# Revit family: xTrench_Drain-Jay R. Smith-9812BS
name_source: partatom
category: Plumbing Fixtures
units: mm (PartAtom-declared; Revit-internal decimal feet)

## family parameters
Always vertical = No
Cut with Voids When Loaded = No
OmniClass Number = 23.70.50.21.24
OmniClass Title = Waste Water Drains
Part Type = Normal
Room Calculation Point = No
Round Connector Dimension = Use Diameter
Shared = Yes
Work Plane-Based = Yes

## types (20) — shared parameters
Assembly Code = D2030300
Body Material = Polyester-Jay R. Smith-Fiberglass
Bottom Outlet = Yes
Bottom Outlet (Specify) = 4 "
CW Connection = No
Description = 10-inch WIDE HIGH CAPACITY PRE-SLOPED FIBERGLASS TRENCH DRAIN SYSTEM
Ductile Iron Slotted Grate = No
End Cap Right = No
Galvanized Steel Bar Grate = No
HW Connection = No
Horizontal Inlet Cap = No
Horizontal Outlet Cap = No
Inlet Size (Specify) = 4 "
Manufacturer = Jay R. Smith
Model = 9812
Opening Inner Rad = 2 "
Opening Outer Rad = 2.25 "
Product Documentation Link = https://www.jrsmith.com
Product URL = https://www.jrsmith.com
Stainless Steel Bar Grate = No
Type Comments = 10-inch WIDE HIGH CAPACITY PRE-SLOPED FIBERGLASS
URL = http://www.jrsmith.com
Universal Deep Closing End Cap = No
Universal Shallow Closing End Cap = No
Vent Connection = No
Waste Connection = Yes
zero-valued in all types: Default Elevation

## per-type parameters (varying)
| type | 108 Channel Rebar | 3N3 Rebar | Bottom Outlet Dist. from Front Inlet | Deep End Depth | J Bend Anchor | Outlet Size (Specify) | Shallow End Depth | Total Length |
| 9812-801 | Yes | No | 59 " | 8 " | Yes | 4 " | 6.88 " | 108 " |
| 9812-802 | Yes | No | 59 " | 9.13 " | Yes | 0 " | 8 " | 108 " |
| 9812-803 | Yes | No | 59 " | 10.25 " | Yes | 0 " | 9.13 " | 108 " |
| 9812-803N | Yes | No | 59 " | 10.25 " | Yes | 0 " | 10.25 " | 108 " |
| 9812-804 | Yes | No | 59 " | 11.38 " | Yes | 0 " | 10.25 " | 108 " |
| 9812-805 | Yes | No | 59 " | 12.5 " | Yes | 0 " | 11.38 " | 108 " |
| 9812-806 | Yes | No | 59 " | 13.63 " | Yes | 0 " | 12.5 " | 108 " |
| 9812-806N | Yes | No | 59 " | 13.63 " | Yes | 0 " | 13.63 " | 108 " |
| 9812-807 | Yes | No | 59 " | 14.75 " | Yes | 0 " | 13.63 " | 108 " |
| 9812-808 | Yes | No | 59 " | 15.88 " | Yes | 0 " | 14.75 " | 108 " |
| 9812-809N | Yes | No | 59 " | 17 " | Yes | 0 " | 17 " | 108 " |
| 9812-810 | Yes | No | 59 " | 18.13 " | Yes | 0 " | 17 " | 108 " |
| 9812-811 | Yes | No | 59 " | 19.25 " | Yes | 0 " | 18.13 " | 108 " |
| 9812-812 | Yes | No | 59 " | 20.38 " | Yes | 0 " | 19.25 " | 108 " |
| 9812-812N | Yes | No | 59 " | 20.38 " | Yes | 0 " | 20.38 " | 108 " |
| 9812-809 | Yes | No | 59 " | 17 " | Yes | 0 " | 15.88 " | 108 " |
| 9812-803N3 | No | Yes | 25 " | 10.25 " | No | 0 " | 10.25 " | 36 " |
| 9812-806N3 | No | Yes | 25 " | 13.63 " | No | 0 " | 13.63 " | 36 " |
| 9812-809N3 | No | Yes | 25 " | 17 " | No | 0 " | 17 " | 36 " |
| 9812-812N3 | No | Yes | 25 " | 20.38 " | No | 0 " | 20.38 " | 36 " |

## geometry (parser evidence)
native form markers: Sweep x3
no freeform markers — native parametric forms only
